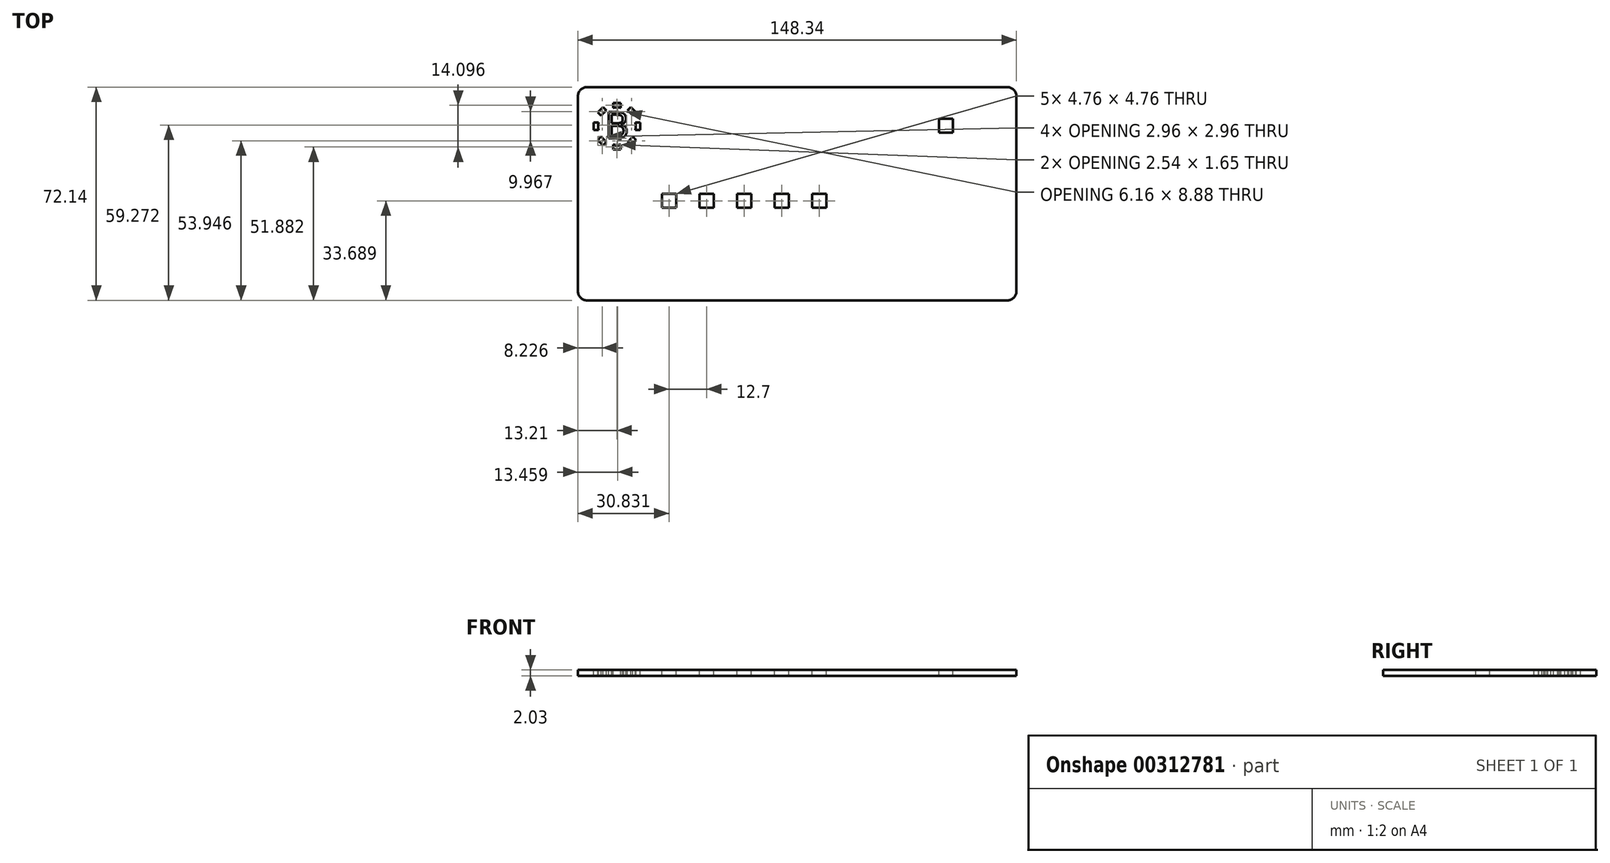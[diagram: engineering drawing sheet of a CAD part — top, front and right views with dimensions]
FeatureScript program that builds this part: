
annotation { "Feature Type Name" : "Feature", "Feature Type Description" : "" }
export const myFeature = defineFeature(function(context is Context, id is Id, definition is map)
    precondition{}
    {
        {
            var Q0;
            Q0=qCreatedBy(makeId("Top.planeOp"),FACE);
            var sketch = newSketch(context, id + "F0", { "sketchPlane" : qUnion([Q0])});
            skLineSegment(sketch, "E0", {"start": v(0, 0) * mm, "end": v(3.05, 0) * mm});
            skLineSegment(sketch, "E1", {"start": v(0, 0) * mm, "end": v(0, 3.05) * mm});
            skArc(sketch, "E2", {"start": v(3.05, 0) * mm, "mid": v(2.16, 2.16) * mm, "end": v(0, 3.05) * mm});
            skLineSegment(sketch, "E3", {"start": v(0, 3.05) * mm, "end": v(-142.24, 3.05) * mm});
            skLineSegment(sketch, "E4", {"start": v(3.05, 0) * mm, "end": v(3.05, -66.04) * mm});
            skLineSegment(sketch, "E5", {"start": v(-71.12, 0) * mm, "end": v(-71.12, -33.02) * mm});
            skPoint(sketch, "E5.startSnap0", {"position": v(-71.12, 3.05) * mm});
            skPoint(sketch, "E5.endSnap0", {"position": v(3.05, -33.02) * mm});
            skLineSegment(sketch, "E6", {"start": v(-71.12, -33.02) * mm, "end": v(3.05, -33.02) * mm});
            skLineSegment(sketch, "E7.MirrorCS", {"start": v(0, -69.09) * mm, "end": v(-142.24, -69.09) * mm});
            skArc(sketch, "E8.MirrorCS", {"start": v(3.05, -66.04) * mm, "mid": v(2.16, -68.2) * mm, "end": v(0, -69.09) * mm});
            skLineSegment(sketch, "E9.MirrorCS", {"start": v(3.05, -66.04) * mm, "end": v(3.05, 0) * mm});
            skLineSegment(sketch, "E10.MirrorCS", {"start": v(-145.29, -66.04) * mm, "end": v(-145.29, 0) * mm});
            skArc(sketch, "E11.MirrorCS", {"start": v(-145.29, -66.04) * mm, "mid": v(-144.4, -68.2) * mm, "end": v(-142.24, -69.09) * mm});
            skArc(sketch, "E12.MirrorCS", {"start": v(-145.29, 0) * mm, "mid": v(-144.4, 2.16) * mm, "end": v(-142.24, 3.05) * mm});
            skSolve(sketch);
        }
        {
            var Q0;
            {var subQ0=sQuery(id+"F0.wireOp",EDGE,"E0");Q0=makeQuery(id+"F0.imprint","IMPRINT",FACE,{"disambiguationData":[TD([[makeQuery(id+"F0.imprint","IMPRINT",EDGE,{"derivedFrom":subQ0}),-1.0]])]});}
            var Q1;
            Q1=makeQuery(id+"F0.imprint","IMPRINT",FACE,{"disambiguationData":[TD([[makeQuery(id+"F0.imprint","IMPRINT",EDGE,{"derivedFrom":sQuery(id+"F0.wireOp",EDGE,"E0")}),1.0]])]});
            extrude(context, id + "F1", {"entities" : qUnion([Q0, Q1]), "depth" : 2.03 * mm});
        }
        {
            var Q0;
            Q0=makeQuery(id+"F1.opExtrude","CAP_FACE",FACE,{"disambiguationData":[OSD([sQuery(id+"F0.wireOp",EDGE,"E0"),sQuery(id+"F0.wireOp",EDGE,"E1"),sQuery(id+"F0.wireOp",EDGE,"E3"),sQuery(id+"F0.wireOp",EDGE,"E7.MirrorCS"),sQuery(id+"F0.wireOp",EDGE,"E8.MirrorCS"),sQuery(id+"F0.wireOp",EDGE,"E9.MirrorCS"),sQuery(id+"F0.wireOp",EDGE,"E10.MirrorCS"),sQuery(id+"F0.wireOp",EDGE,"E11.MirrorCS"),sQuery(id+"F0.wireOp",EDGE,"E12.MirrorCS")])],"isStart":false});
            var sketch = newSketch(context, id + "F2", { "sketchPlane" : qUnion([Q0])});
            skLineSegment(sketch, "E13", {"start": v(-145.29, 0) * mm, "end": v(3.05, 0) * mm});
            skLineSegment(sketch, "E14", {"start": v(-142.24, 3.05) * mm, "end": v(-142.24, -69.09) * mm});
            skLineSegment(sketch, "E15", {"start": v(-145.29, -66.04) * mm, "end": v(3.05, -66.04) * mm});
            skLineSegment(sketch, "E16", {"start": v(0, -69.09) * mm, "end": v(0, 3.05) * mm});
            skLineSegment(sketch, "E17.bottom", {"start": v(-142.24, 0) * mm, "end": v(-121.92, 0) * mm});
            skLineSegment(sketch, "E17.top", {"start": v(-142.24, -20.32) * mm, "end": v(-121.92, -20.32) * mm});
            skLineSegment(sketch, "E17.left", {"start": v(-142.24, 0) * mm, "end": v(-142.24, -20.32) * mm});
            skLineSegment(sketch, "E17.right", {"start": v(-121.92, 0) * mm, "end": v(-121.92, -20.32) * mm});
            skCircle(sketch, "E18", {"center": v(-132.08, -10.16) * mm, "radius": 6.35 * mm});
            skPoint(sketch, "E18.centerSnap0", {"position": v(-121.92, -10.16) * mm});
            skPoint(sketch, "E18.centerSnap1", {"position": v(-132.08, 0) * mm});
            skLineSegment(sketch, "E19", {"start": v(-132.08, -3.81) * mm, "end": v(-132.08, -2.29) * mm});
            skLineSegment(sketch, "E20", {"start": v(-132.08, -2.29) * mm, "end": v(-130.8, -2.29) * mm});
            skLineSegment(sketch, "E21", {"start": v(-130.8, -2.29) * mm, "end": v(-130.8, -3.94) * mm});
            skLineSegment(sketch, "E22.MirrorCS", {"start": v(-133.35, -2.29) * mm, "end": v(-133.35, -3.94) * mm});
            skLineSegment(sketch, "E23.MirrorCS", {"start": v(-132.08, -2.29) * mm, "end": v(-133.35, -2.29) * mm});
            skLineSegment(sketch, "E24.1.0", {"start": v(-136.75, -3.7) * mm, "end": v(-135.58, -4.86) * mm});
            skLineSegment(sketch, "E24.1.1", {"start": v(-138.55, -5.5) * mm, "end": v(-137.38, -6.66) * mm});
            skLineSegment(sketch, "E24.1.2", {"start": v(-137.65, -4.6) * mm, "end": v(-138.55, -5.5) * mm});
            skLineSegment(sketch, "E24.1.3", {"start": v(-137.65, -4.6) * mm, "end": v(-136.75, -3.7) * mm});
            skLineSegment(sketch, "E24.2.0", {"start": v(-139.95, -8.9) * mm, "end": v(-138.3, -8.9) * mm});
            skLineSegment(sketch, "E24.2.1", {"start": v(-139.95, -11.43) * mm, "end": v(-138.3, -11.43) * mm});
            skLineSegment(sketch, "E24.2.2", {"start": v(-139.95, -10.16) * mm, "end": v(-139.95, -11.43) * mm});
            skLineSegment(sketch, "E24.2.3", {"start": v(-139.95, -10.16) * mm, "end": v(-139.95, -8.9) * mm});
            skLineSegment(sketch, "E24.3.0", {"start": v(-138.55, -14.83) * mm, "end": v(-137.38, -13.66) * mm});
            skLineSegment(sketch, "E24.3.1", {"start": v(-136.75, -16.63) * mm, "end": v(-135.58, -15.46) * mm});
            skLineSegment(sketch, "E24.3.2", {"start": v(-137.65, -15.73) * mm, "end": v(-136.75, -16.63) * mm});
            skLineSegment(sketch, "E24.3.3", {"start": v(-137.65, -15.73) * mm, "end": v(-138.55, -14.83) * mm});
            skLineSegment(sketch, "E24.4.0", {"start": v(-133.35, -18.03) * mm, "end": v(-133.35, -16.38) * mm});
            skLineSegment(sketch, "E24.4.1", {"start": v(-130.8, -18.03) * mm, "end": v(-130.8, -16.38) * mm});
            skLineSegment(sketch, "E24.4.2", {"start": v(-132.08, -18.03) * mm, "end": v(-130.8, -18.03) * mm});
            skLineSegment(sketch, "E24.4.3", {"start": v(-132.08, -18.03) * mm, "end": v(-133.35, -18.03) * mm});
            skLineSegment(sketch, "E24.5.0", {"start": v(-127.41, -16.63) * mm, "end": v(-128.58, -15.46) * mm});
            skLineSegment(sketch, "E24.5.1", {"start": v(-125.61, -14.83) * mm, "end": v(-126.78, -13.66) * mm});
            skLineSegment(sketch, "E24.5.2", {"start": v(-126.51, -15.73) * mm, "end": v(-125.61, -14.83) * mm});
            skLineSegment(sketch, "E24.5.3", {"start": v(-126.51, -15.73) * mm, "end": v(-127.41, -16.63) * mm});
            skLineSegment(sketch, "E24.6.0", {"start": v(-124.2, -11.43) * mm, "end": v(-125.86, -11.43) * mm});
            skLineSegment(sketch, "E24.6.1", {"start": v(-124.2, -8.9) * mm, "end": v(-125.86, -8.9) * mm});
            skLineSegment(sketch, "E24.6.2", {"start": v(-124.2, -10.16) * mm, "end": v(-124.2, -8.9) * mm});
            skLineSegment(sketch, "E24.6.3", {"start": v(-124.2, -10.16) * mm, "end": v(-124.2, -11.43) * mm});
            skLineSegment(sketch, "E24.7.0", {"start": v(-125.61, -5.5) * mm, "end": v(-126.78, -6.66) * mm});
            skLineSegment(sketch, "E24.7.1", {"start": v(-127.41, -3.7) * mm, "end": v(-128.58, -4.86) * mm});
            skLineSegment(sketch, "E24.7.2", {"start": v(-126.51, -4.6) * mm, "end": v(-127.41, -3.7) * mm});
            skLineSegment(sketch, "E24.7.3", {"start": v(-126.51, -4.6) * mm, "end": v(-125.61, -5.5) * mm});
            skText(sketch, "E25", { "text": "B\n", "fontName": "OpenSans-Regular.ttf"});
            skCircle(sketch, "E26", {"center": v(-132.08, -10.16) * mm, "radius": 5.59 * mm});
            const initialGuessF2  = {"E25": [-0.13613, -0.01426, 1, 0, 0.00896]};
            skSetInitialGuess(sketch, initialGuessF2);
            skSolve(sketch);
        }
        {
            var Q0;
            {var subQ1=sQuery(id+"F2.wireOp",EDGE,"E24.1.0");Q0=makeQuery(id+"F2.imprint","IMPRINT",FACE,{"disambiguationData":[TD([[makeQuery(id+"F2.imprint","IMPRINT",EDGE,{"derivedFrom":subQ1}),-1.0]])]});}
            var Q1;
            {var subQ0=sQuery(id+"F2.wireOp",EDGE,"E19");Q1=makeQuery(id+"F2.imprint","IMPRINT",FACE,{"disambiguationData":[TD([[makeQuery(id+"F2.imprint","IMPRINT",EDGE,{"derivedFrom":subQ0}),-1.0]])]});}
            var Q2;
            {var subQ0=sQuery(id+"F2.wireOp",EDGE,"E19");Q2=makeQuery(id+"F2.imprint","IMPRINT",FACE,{"disambiguationData":[TD([[makeQuery(id+"F2.imprint","IMPRINT",EDGE,{"derivedFrom":subQ0}),1.0]])]});}
            var Q3;
            {var subQ1=sQuery(id+"F2.wireOp",EDGE,"E24.7.0");Q3=makeQuery(id+"F2.imprint","IMPRINT",FACE,{"disambiguationData":[TD([[makeQuery(id+"F2.imprint","IMPRINT",EDGE,{"derivedFrom":subQ1}),-1.0]])]});}
            var Q4;
            {var subQ1=sQuery(id+"F2.wireOp",EDGE,"E24.6.0");Q4=makeQuery(id+"F2.imprint","IMPRINT",FACE,{"disambiguationData":[TD([[makeQuery(id+"F2.imprint","IMPRINT",EDGE,{"derivedFrom":subQ1}),-1.0]])]});}
            var Q5;
            {var subQ0=sQuery(id+"F2.wireOp",EDGE,"E24.5.0");Q5=makeQuery(id+"F2.imprint","IMPRINT",FACE,{"disambiguationData":[TD([[makeQuery(id+"F2.imprint","IMPRINT",EDGE,{"derivedFrom":subQ0}),-1.0]])]});}
            var Q6;
            {var subQ1=sQuery(id+"F2.wireOp",EDGE,"E24.4.0");Q6=makeQuery(id+"F2.imprint","IMPRINT",FACE,{"disambiguationData":[TD([[makeQuery(id+"F2.imprint","IMPRINT",EDGE,{"derivedFrom":subQ1}),-1.0]])]});}
            var Q7;
            {var subQ0=sQuery(id+"F2.wireOp",EDGE,"E24.3.0");Q7=makeQuery(id+"F2.imprint","IMPRINT",FACE,{"disambiguationData":[TD([[makeQuery(id+"F2.imprint","IMPRINT",EDGE,{"derivedFrom":subQ0}),-1.0]])]});}
            var Q8;
            {var subQ1=sQuery(id+"F2.wireOp",EDGE,"E24.2.0");Q8=makeQuery(id+"F2.imprint","IMPRINT",FACE,{"disambiguationData":[TD([[makeQuery(id+"F2.imprint","IMPRINT",EDGE,{"derivedFrom":subQ1}),-1.0]])]});}
            var Q9;
            Q9=makeQuery(id+"F2.imprint","IMPRINT",FACE,{"disambiguationData":[TD([[makeQuery(id+"F2.imprint","IMPRINT",EDGE,{"derivedFrom":sQuery(id+"F2.wireOp",EDGE,"E25.sketch_text.stroke-0")}),-1.0]])]});
            extrude(context, id + "F3", {"entities" : qUnion([Q0, Q1, Q2, Q3, Q4, Q5, Q6, Q7, Q8, Q9]), "operationType" : NewBodyOperationType.REMOVE, "oppositeDirection" : true, "depth" : 2.03 * mm});
        }
        {
            var Q0;
            {var subQ13=sQuery(id+"F0.wireOp",EDGE,"E7.MirrorCS");var subQ14=sQuery(id+"F0.wireOp",EDGE,"E12.MirrorCS");var subQ16=sQuery(id+"F0.wireOp",EDGE,"E11.MirrorCS");var subQ21=sQuery(id+"F0.wireOp",EDGE,"E10.MirrorCS");var subQ22=sQuery(id+"F0.wireOp",EDGE,"E9.MirrorCS");var subQ23=sQuery(id+"F0.wireOp",EDGE,"E2");var subQ24=sQuery(id+"F0.wireOp",EDGE,"E8.MirrorCS");var subQ25=sQuery(id+"F0.wireOp",EDGE,"E3");Q0=makeQuery(id+"F3.boolean.opBoolean","SPLIT",FACE,{"disambiguationData":[TD([makeQuery(id+"F1.opExtrude","SWEPT_FACE",FACE,{"disambiguationData":[OSD([subQ23])]})])],"derivedFrom":makeQuery(id+"F1.opExtrude","CAP_FACE",FACE,{"disambiguationData":[OSD([subQ23,subQ25,subQ13,subQ24,subQ22,subQ21,subQ16,subQ14])],"isStart":false})});}
            var sketch = newSketch(context, id + "F4", { "sketchPlane" : qUnion([Q0])});
            skLineSegment(sketch, "E27", {"start": v(-142.24, 3.05) * mm, "end": v(-142.24, -69.09) * mm});
            skLineSegment(sketch, "E28", {"start": v(-145.29, -66.04) * mm, "end": v(3.05, -66.04) * mm});
            skLineSegment(sketch, "E29", {"start": v(0, -69.09) * mm, "end": v(0, 3.05) * mm});
            skLineSegment(sketch, "E30", {"start": v(-116.84, 0) * mm, "end": v(-116.84, -66.04) * mm});
            skLineSegment(sketch, "E31.bottom", {"start": v(-116.84, -33.02) * mm, "end": v(-112.08, -33.02) * mm});
            skLineSegment(sketch, "E31.top", {"start": v(-116.84, -37.78) * mm, "end": v(-112.08, -37.78) * mm});
            skLineSegment(sketch, "E31.left", {"start": v(-116.84, -33.02) * mm, "end": v(-116.84, -37.78) * mm});
            skLineSegment(sketch, "E31.right", {"start": v(-112.08, -33.02) * mm, "end": v(-112.08, -37.78) * mm});
            skLineSegment(sketch, "E32.bottom", {"start": v(-104.14, -33.02) * mm, "end": v(-99.38, -33.02) * mm});
            skLineSegment(sketch, "E32.top", {"start": v(-104.14, -37.78) * mm, "end": v(-99.38, -37.78) * mm});
            skLineSegment(sketch, "E32.left", {"start": v(-104.14, -33.02) * mm, "end": v(-104.14, -37.78) * mm});
            skLineSegment(sketch, "E32.right", {"start": v(-99.38, -33.02) * mm, "end": v(-99.38, -37.78) * mm});
            skLineSegment(sketch, "E33.bottom", {"start": v(-91.44, -33.02) * mm, "end": v(-86.68, -33.02) * mm});
            skLineSegment(sketch, "E33.top", {"start": v(-91.44, -37.78) * mm, "end": v(-86.68, -37.78) * mm});
            skLineSegment(sketch, "E33.left", {"start": v(-91.44, -33.02) * mm, "end": v(-91.44, -37.78) * mm});
            skLineSegment(sketch, "E33.right", {"start": v(-86.68, -33.02) * mm, "end": v(-86.68, -37.78) * mm});
            skLineSegment(sketch, "E34.bottom", {"start": v(-78.74, -33.02) * mm, "end": v(-73.98, -33.02) * mm});
            skLineSegment(sketch, "E34.top", {"start": v(-78.74, -37.78) * mm, "end": v(-73.98, -37.78) * mm});
            skLineSegment(sketch, "E34.left", {"start": v(-78.74, -33.02) * mm, "end": v(-78.74, -37.78) * mm});
            skLineSegment(sketch, "E34.right", {"start": v(-73.98, -33.02) * mm, "end": v(-73.98, -37.78) * mm});
            skLineSegment(sketch, "E35.bottom", {"start": v(-66.04, -33.02) * mm, "end": v(-61.28, -33.02) * mm});
            skLineSegment(sketch, "E35.top", {"start": v(-66.04, -37.78) * mm, "end": v(-61.28, -37.78) * mm});
            skLineSegment(sketch, "E35.left", {"start": v(-66.04, -33.02) * mm, "end": v(-66.04, -37.78) * mm});
            skLineSegment(sketch, "E35.right", {"start": v(-61.28, -33.02) * mm, "end": v(-61.28, -37.78) * mm});
            skLineSegment(sketch, "E36", {"start": v(-61.28, -66.04) * mm, "end": v(-23.18, -66.04) * mm});
            skLineSegment(sketch, "E37", {"start": v(-116.84, -33.02) * mm, "end": v(-116.84, -6.24) * mm});
            skLineSegment(sketch, "E38", {"start": v(-61.28, -33.02) * mm, "end": v(-61.28, -7.62) * mm});
            skLineSegment(sketch, "E39.bottom", {"start": v(-23.18, -7.62) * mm, "end": v(-18.4, -7.62) * mm});
            skLineSegment(sketch, "E39.top", {"start": v(-23.18, -12.4) * mm, "end": v(-18.4, -12.4) * mm});
            skLineSegment(sketch, "E39.left", {"start": v(-23.18, -7.62) * mm, "end": v(-23.18, -12.4) * mm});
            skLineSegment(sketch, "E39.right", {"start": v(-18.4, -7.62) * mm, "end": v(-18.4, -12.4) * mm});
            skSolve(sketch);
        }
        {
            var Q0;
            Q0=makeQuery(id+"F4.imprint","IMPRINT",FACE,{"disambiguationData":[TD([[makeQuery(id+"F4.imprint","IMPRINT",EDGE,{"derivedFrom":sQuery(id+"F4.wireOp",EDGE,"E31.bottom")}),-1.0]])]});
            var Q1;
            Q1=makeQuery(id+"F4.imprint","IMPRINT",FACE,{"disambiguationData":[TD([[makeQuery(id+"F4.imprint","IMPRINT",EDGE,{"derivedFrom":sQuery(id+"F4.wireOp",EDGE,"E32.bottom")}),-1.0]])]});
            var Q2;
            Q2=makeQuery(id+"F4.imprint","IMPRINT",FACE,{"disambiguationData":[TD([[makeQuery(id+"F4.imprint","IMPRINT",EDGE,{"derivedFrom":sQuery(id+"F4.wireOp",EDGE,"E33.bottom")}),-1.0]])]});
            var Q3;
            Q3=makeQuery(id+"F4.imprint","IMPRINT",FACE,{"disambiguationData":[TD([[makeQuery(id+"F4.imprint","IMPRINT",EDGE,{"derivedFrom":sQuery(id+"F4.wireOp",EDGE,"E34.bottom")}),-1.0]])]});
            var Q4;
            Q4=makeQuery(id+"F4.imprint","IMPRINT",FACE,{"disambiguationData":[TD([[makeQuery(id+"F4.imprint","IMPRINT",EDGE,{"derivedFrom":sQuery(id+"F4.wireOp",EDGE,"E35.bottom")}),-1.0]])]});
            var Q5;
            Q5=makeQuery(id+"F4.imprint","IMPRINT",FACE,{"disambiguationData":[TD([[makeQuery(id+"F4.imprint","IMPRINT",EDGE,{"derivedFrom":sQuery(id+"F4.wireOp",EDGE,"E39.bottom")}),-1.0]])]});
            extrude(context, id + "F5", {"entities" : qUnion([Q0, Q1, Q2, Q3, Q4, Q5]), "operationType" : NewBodyOperationType.REMOVE, "oppositeDirection" : true, "depth" : 2.03 * mm});
        }
    });
